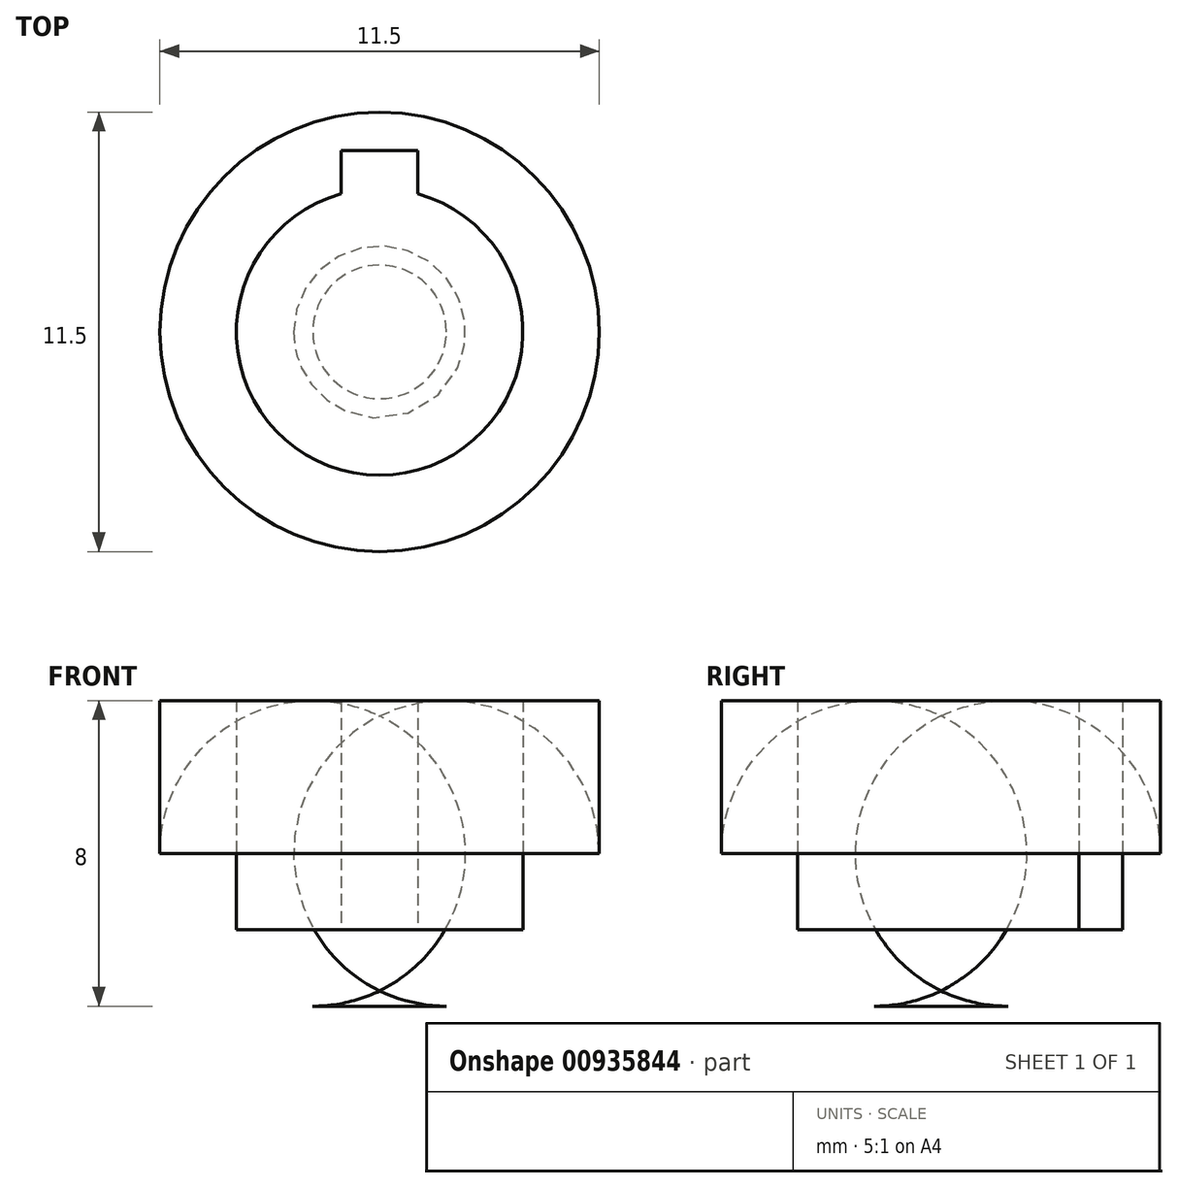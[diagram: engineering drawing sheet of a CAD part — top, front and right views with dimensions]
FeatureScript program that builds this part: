
annotation { "Feature Type Name" : "Feature", "Feature Type Description" : "" }
export const myFeature = defineFeature(function(context is Context, id is Id, definition is map)
    precondition{}
    {
        {
            var Q0;
            Q0=qCreatedBy(makeId("Top.planeOp"),FACE);
            var sketch = newSketch(context, id + "F0", { "sketchPlane" : qUnion([Q0])});
            skCircle(sketch, "E0", {"center": v(0, 0) * mm, "radius": 3.75 * mm});
            skCircle(sketch, "E1", {"center": v(0, 0) * mm, "radius": 5.75 * mm});
            skLineSegment(sketch, "E2.bottom", {"start": v(1, 2.75) * mm, "end": v(-1, 2.75) * mm});
            skLineSegment(sketch, "E2.top", {"start": v(1, 4.75) * mm, "end": v(-1, 4.75) * mm});
            skLineSegment(sketch, "E2.left", {"start": v(1, 2.75) * mm, "end": v(1, 4.75) * mm});
            skLineSegment(sketch, "E2.right", {"start": v(-1, 2.75) * mm, "end": v(-1, 4.75) * mm});
            skPoint(sketch, "E2.middle", {"position": v(0, 3.75) * mm});
            skPoint(sketch, "E3.middle", {"position": v(0, 1.22) * mm});
            skSolve(sketch);
        }
        {
            var Q0;
            Q0=makeQuery(id+"F0.imprint","IMPRINT",FACE,{"disambiguationData":[TD([[makeQuery(id+"F0.imprint","IMPRINT",EDGE,{"derivedFrom":sQuery(id+"F0.wireOp",EDGE,"E1")}),1.0]])]});
            extrude(context, id + "F1", {"entities" : qUnion([Q0]), "depth" : 8 * mm, "offsetDistance" : 25 * mm});
        }
        {
            var Q0;
            {var subQ5=sQuery(id+"F0.wireOp",EDGE,"E2.bottom");Q0=makeQuery(id+"F0.imprint","IMPRINT",FACE,{"disambiguationData":[TD([[makeQuery(id+"F0.imprint","IMPRINT",EDGE,{"derivedFrom":subQ5}),1.0]])]});}
            var Q1;
            {var subQ5=sQuery(id+"F0.wireOp",EDGE,"E2.bottom");Q1=makeQuery(id+"F0.imprint","IMPRINT",FACE,{"disambiguationData":[TD([[makeQuery(id+"F0.imprint","IMPRINT",EDGE,{"derivedFrom":subQ5}),-1.0]])]});}
            var Q2;
            {var subQ5=sQuery(id+"F0.wireOp",EDGE,"E2.top");Q2=makeQuery(id+"F0.imprint","IMPRINT",FACE,{"disambiguationData":[TD([[makeQuery(id+"F0.imprint","IMPRINT",EDGE,{"derivedFrom":subQ5}),1.0]])]});}
            extrude(context, id + "F2", {"entities" : qUnion([Q0, Q1, Q2]), "operationType" : NewBodyOperationType.ADD, "depth" : 2 * mm, "offsetDistance" : 25 * mm});
        }
        {
            var Q0;
            Q0=makeQuery(id+"F1.opExtrude","CAP_EDGE",EDGE,{"disambiguationData":[OSD([sQuery(id+"F0.wireOp",EDGE,"E1")])],"isStart":true});
            fillet(context, id + "F3", {"entities" : qUnion([Q0]), "radius" : 4 * mm, "tangentPropagation" : true, "allowEdgeOverflow" : false});
        }
    });
